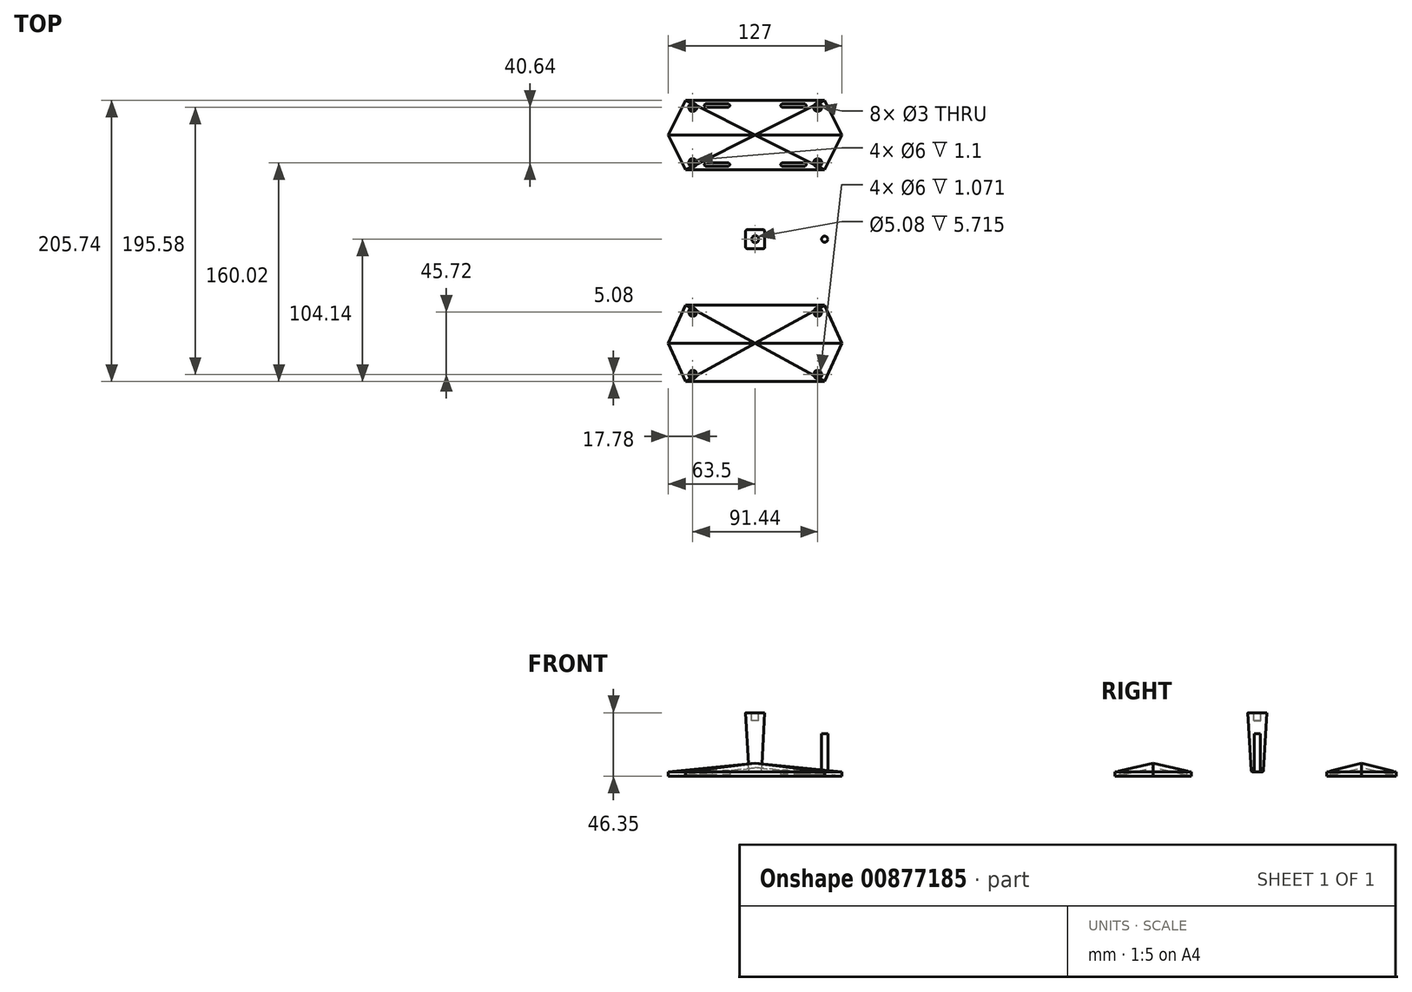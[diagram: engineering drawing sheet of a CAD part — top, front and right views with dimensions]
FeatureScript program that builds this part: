
annotation { "Feature Type Name" : "Feature", "Feature Type Description" : "" }
export const myFeature = defineFeature(function(context is Context, id is Id, definition is map)
    precondition{}
    {
        {
            var Q0;
            Q0=qCreatedBy(makeId("Top.planeOp"),FACE);
            var sketch = newSketch(context, id + "F0", { "sketchPlane" : qUnion([Q0])});
            skLineSegment(sketch, "E0", {"start": v(0, 0) * mm, "end": v(0, -76.2) * mm, "construction": true});
            skLineSegment(sketch, "E1.bottom", {"start": v(50.8, -48.26) * mm, "end": v(-50.8, -48.26) * mm});
            skLineSegment(sketch, "E1.top", {"start": v(50.8, -104.14) * mm, "end": v(-50.8, -104.14) * mm});
            skLineSegment(sketch, "E1.left", {"start": v(50.8, -48.26) * mm, "end": v(50.8, -104.14) * mm, "construction": true});
            skLineSegment(sketch, "E1.right", {"start": v(-50.8, -48.26) * mm, "end": v(-50.8, -104.14) * mm, "construction": true});
            skPoint(sketch, "E1.middle", {"position": v(0, -76.2) * mm});
            skLineSegment(sketch, "E2", {"start": v(50.8, -76.2) * mm, "end": v(63.5, -76.2) * mm, "construction": true});
            skLineSegment(sketch, "E3", {"start": v(63.5, -76.2) * mm, "end": v(50.8, -48.26) * mm});
            skLineSegment(sketch, "E4", {"start": v(50.8, -104.14) * mm, "end": v(63.5, -76.2) * mm});
            skLineSegment(sketch, "E5.MirrorCS", {"start": v(-63.5, -76.2) * mm, "end": v(-50.8, -48.26) * mm});
            skLineSegment(sketch, "E6.MirrorCS", {"start": v(-50.8, -104.14) * mm, "end": v(-63.5, -76.2) * mm});
            skSolve(sketch);
        }
        {
            var Q0;
            Q0=qCreatedBy(makeId("Right.planeOp"),FACE);
            var sketch = newSketch(context, id + "F1", { "sketchPlane" : qUnion([Q0])});
            skLineSegment(sketch, "E7", {"start": v(0, 0) * mm, "end": v(-76.2, 0) * mm, "construction": true});
            skLineSegment(sketch, "E8", {"start": v(-76.2, 0) * mm, "end": v(-76.2, 6.35) * mm, "construction": true});
            skLineSegment(sketch, "E9", {"start": v(-76.2, 0) * mm, "end": v(-76.2, 3.17) * mm, "construction": true});
            skLineSegment(sketch, "E10", {"start": v(0, 0) * mm, "end": v(76.2, 0) * mm, "construction": true});
            skLineSegment(sketch, "E11", {"start": v(76.2, 0) * mm, "end": v(76.2, 6.35) * mm, "construction": true});
            skSolve(sketch);
        }
        {
            var Q0;
            Q0=makeQuery(id+"F0.imprint","IMPRINT",FACE,{"disambiguationData":[TD([[makeQuery(id+"F0.imprint","IMPRINT",EDGE,{"derivedFrom":sQuery(id+"F0.wireOp",EDGE,"E1.bottom")}),1.0]])]});
            var Q1;
            Q1=sQuery(id+"F1.wireOp",VERTEX,"E8.end");
            loft(context, id + "F2", {"sheetProfilesArray" : [{ "sheetProfileEntities" : qUnion([Q0]) }, { "sheetProfileEntities" : qUnion([Q1]) }]});
        }
        {
            var Q0;
            Q0=qCreatedBy(makeId("Right.planeOp"),FACE);
            var sketch = newSketch(context, id + "F3", { "sketchPlane" : qUnion([Q0])});
            skLineSegment(sketch, "E12", {"start": v(0, 0) * mm, "end": v(-76.2, 0) * mm, "construction": true});
            skLineSegment(sketch, "E13", {"start": v(-76.2, 0) * mm, "end": v(-76.2, 3.17) * mm, "construction": true});
            skLineSegment(sketch, "E14", {"start": v(0, 0) * mm, "end": v(76.2, 0) * mm, "construction": true});
            skLineSegment(sketch, "E15", {"start": v(76.2, 0) * mm, "end": v(76.2, 3.18) * mm, "construction": true});
            skSolve(sketch);
        }
        {
            var Q0;
            Q0=qSketchRegion(id+"F0",true);
            extrude(context, id + "F4", {"entities" : qUnion([Q0]), "operationType" : NewBodyOperationType.ADD, "oppositeDirection" : true, "depth" : 3 * mm, "offsetDistance" : 25.4 * mm});
        }
        {
            var Q1;
            Q1=makeQuery(id+"F4.opExtrude","CAP_FACE",FACE,{"disambiguationData":[OSD([sQuery(id+"F0.wireOp",EDGE,"E1.bottom"),sQuery(id+"F0.wireOp",EDGE,"E1.top"),sQuery(id+"F0.wireOp",EDGE,"E3"),sQuery(id+"F0.wireOp",EDGE,"E4"),sQuery(id+"F0.wireOp",EDGE,"E5.MirrorCS"),sQuery(id+"F0.wireOp",EDGE,"E6.MirrorCS")])],"isStart":false});
            var Q2;
            Q2=sQuery(id+"F1.wireOp",VERTEX,"E9.end");
            loft(context, id + "F5", {"operationType" : NewBodyOperationType.REMOVE, "sheetProfilesArray" : [{ "sheetProfileEntities" : qUnion([Q1]) }, { "sheetProfileEntities" : qUnion([Q2]) }]});
        }
        {
            var Q0;
            Q0=qCreatedBy(makeId("Top.planeOp"),FACE);
            var sketch = newSketch(context, id + "F6", { "sketchPlane" : qUnion([Q0])});
            skLineSegment(sketch, "E16", {"start": v(0, 0) * mm, "end": v(0, -76.2) * mm, "construction": true});
            skLineSegment(sketch, "E17", {"start": v(0, -76.2) * mm, "end": v(50.8, -76.2) * mm, "construction": true});
            skLineSegment(sketch, "E18", {"start": v(50.8, -76.2) * mm, "end": v(50.8, -48.26) * mm, "construction": true});
            skLineSegment(sketch, "E19.bottom", {"start": v(50.8, -48.26) * mm, "end": v(45.72, -48.26) * mm, "construction": true});
            skLineSegment(sketch, "E19.top", {"start": v(50.8, -53.34) * mm, "end": v(45.72, -53.34) * mm, "construction": true});
            skLineSegment(sketch, "E19.left", {"start": v(50.8, -48.26) * mm, "end": v(50.8, -53.34) * mm, "construction": true});
            skLineSegment(sketch, "E19.right", {"start": v(45.72, -48.26) * mm, "end": v(45.72, -53.34) * mm, "construction": true});
            skCircle(sketch, "E20", {"center": v(45.72, -53.34) * mm, "radius": 1.5 * mm});
            skCircle(sketch, "E21.MirrorC", {"center": v(-45.72, -53.34) * mm, "radius": 1.5 * mm});
            skCircle(sketch, "E22.MirrorC", {"center": v(45.72, -99.06) * mm, "radius": 1.5 * mm});
            skCircle(sketch, "E23.MirrorC", {"center": v(-45.72, -99.06) * mm, "radius": 1.5 * mm});
            skSolve(sketch);
        }
        {
            var Q0;
            Q0=makeQuery(id+"F6.imprint","IMPRINT",FACE,{"disambiguationData":[TD([[makeQuery(id+"F6.imprint","IMPRINT",EDGE,{"derivedFrom":sQuery(id+"F6.wireOp",EDGE,"E20")}),1.0]])]});
            var Q1;
            Q1=makeQuery(id+"F6.imprint","IMPRINT",FACE,{"disambiguationData":[TD([[makeQuery(id+"F6.imprint","IMPRINT",EDGE,{"derivedFrom":sQuery(id+"F6.wireOp",EDGE,"E21.MirrorC")}),-1.0]])]});
            var Q2;
            Q2=makeQuery(id+"F6.imprint","IMPRINT",FACE,{"disambiguationData":[TD([[makeQuery(id+"F6.imprint","IMPRINT",EDGE,{"derivedFrom":sQuery(id+"F6.wireOp",EDGE,"E22.MirrorC")}),-1.0]])]});
            var Q3;
            Q3=makeQuery(id+"F6.imprint","IMPRINT",FACE,{"disambiguationData":[TD([[makeQuery(id+"F6.imprint","IMPRINT",EDGE,{"derivedFrom":sQuery(id+"F6.wireOp",EDGE,"E23.MirrorC")}),1.0]])]});
            var Q4;
            Q4=makeQuery(id+"F6.imprint","IMPRINT",FACE,{"disambiguationData":[TD([[makeQuery(id+"F6.imprint","IMPRINT",EDGE,{"derivedFrom":sQuery(id+"F6.wireOp",EDGE,"608550e4-dcd5-4afd-8712-c4d8ff7671cc0.MirrorC")}),-1.0]])]});
            var Q5;
            Q5=makeQuery(id+"F6.imprint","IMPRINT",FACE,{"disambiguationData":[TD([[makeQuery(id+"F6.imprint","IMPRINT",EDGE,{"derivedFrom":sQuery(id+"F6.wireOp",EDGE,"e33e717c-8c95-4304-aaaf-b1c399a1f4810.MirrorC")}),-1.0]])]});
            var Q6;
            Q6=makeQuery(id+"F6.imprint","IMPRINT",FACE,{"disambiguationData":[TD([[makeQuery(id+"F6.imprint","IMPRINT",EDGE,{"derivedFrom":sQuery(id+"F6.wireOp",EDGE,"5184385d-e241-4d37-b116-434bd50265c70.MirrorC")}),1.0]])]});
            var Q7;
            Q7=makeQuery(id+"F6.imprint","IMPRINT",FACE,{"disambiguationData":[TD([[makeQuery(id+"F6.imprint","IMPRINT",EDGE,{"derivedFrom":sQuery(id+"F6.wireOp",EDGE,"1d585823-e6b4-4162-827a-ad62070646b00.MirrorC")}),1.0]])]});
            extrude(context, id + "F7", {"entities" : qUnion([Q0, Q1, Q2, Q3, Q4, Q5, Q6, Q7]), "operationType" : NewBodyOperationType.REMOVE, "depth" : 25.4 * mm, "offsetDistance" : 25.4 * mm});
        }
        {
            var Q0;
            Q0=qSketchRegion(id+"F6",true);
            extrude(context, id + "F8", {"entities" : qUnion([Q0]), "operationType" : NewBodyOperationType.REMOVE, "oppositeDirection" : true, "depth" : 25.4 * mm, "offsetDistance" : 25.4 * mm});
        }
        {
            var Q0;
            Q0=qCreatedBy(makeId("Top.planeOp"),FACE);
            var sketch = newSketch(context, id + "F9", { "sketchPlane" : qUnion([Q0])});
            skLineSegment(sketch, "E24", {"start": v(0, 0) * mm, "end": v(0, -76.2) * mm, "construction": true});
            skLineSegment(sketch, "E25", {"start": v(0, -76.2) * mm, "end": v(50.8, -76.2) * mm, "construction": true});
            skLineSegment(sketch, "E26", {"start": v(50.8, -76.2) * mm, "end": v(50.8, -48.26) * mm, "construction": true});
            skLineSegment(sketch, "E27.bottom", {"start": v(50.8, -48.26) * mm, "end": v(45.72, -48.26) * mm, "construction": true});
            skLineSegment(sketch, "E27.top", {"start": v(50.8, -53.34) * mm, "end": v(45.72, -53.34) * mm, "construction": true});
            skLineSegment(sketch, "E27.left", {"start": v(50.8, -48.26) * mm, "end": v(50.8, -53.34) * mm, "construction": true});
            skLineSegment(sketch, "E27.right", {"start": v(45.72, -48.26) * mm, "end": v(45.72, -53.34) * mm, "construction": true});
            skCircle(sketch, "E28", {"center": v(45.72, -53.34) * mm, "radius": 3 * mm});
            skCircle(sketch, "E29", {"center": v(45.72, -53.34) * mm, "radius": 1.5 * mm});
            skCircle(sketch, "E30.MirrorC", {"center": v(45.72, -99.06) * mm, "radius": 1.5 * mm});
            skCircle(sketch, "E31.MirrorC", {"center": v(45.72, -99.06) * mm, "radius": 3 * mm});
            skCircle(sketch, "E32.MirrorC", {"center": v(-45.72, -53.34) * mm, "radius": 3 * mm});
            skCircle(sketch, "E33.MirrorC", {"center": v(-45.72, -53.34) * mm, "radius": 1.5 * mm});
            skCircle(sketch, "E34.MirrorC", {"center": v(-45.72, -99.06) * mm, "radius": 1.5 * mm});
            skCircle(sketch, "E35.MirrorC", {"center": v(-45.72, -99.06) * mm, "radius": 3 * mm});
            skSolve(sketch);
        }
        {
            var Q0;
            Q0=qSketchRegion(id+"F9",true);
            extrude(context, id + "F10", {"entities" : qUnion([Q0]), "operationType" : NewBodyOperationType.ADD, "oppositeDirection" : true, "depth" : 3 * mm, "offsetDistance" : 25.4 * mm});
        }
        {
            var Q0;
            Q0=qCreatedBy(makeId("Top.planeOp"),FACE);
            var sketch = newSketch(context, id + "F11", { "sketchPlane" : qUnion([Q0])});
            skLineSegment(sketch, "E36.bottom", {"start": v(4.45, 4.45) * mm, "end": v(-4.44, 4.45) * mm});
            skLineSegment(sketch, "E36.top", {"start": v(4.44, -4.45) * mm, "end": v(-4.45, -4.45) * mm});
            skLineSegment(sketch, "E36.left", {"start": v(4.45, 4.45) * mm, "end": v(4.45, -4.45) * mm});
            skLineSegment(sketch, "E36.right", {"start": v(-4.45, 4.45) * mm, "end": v(-4.45, -4.45) * mm});
            skPoint(sketch, "E36.middle", {"position": v(0, 0) * mm});
            skSolve(sketch);
        }
        {
            var Q0;
            Q0=qCreatedBy(makeId("Top.planeOp"),FACE);
            cPlane(context, id + "F12", {"entities" : qUnion([Q0]), "cplaneType" : CPlaneType.OFFSET, "offset" : 28 * mm + 6.35 * mm + 3 * mm + 6 * mm, "width" : 152.4 * mm, "height" : 152.4 * mm});
        }
        {
            var Q0;
            Q0=qCreatedBy(id+"F12.planeOp",FACE);
            var sketch = newSketch(context, id + "F13", { "sketchPlane" : qUnion([Q0])});
            skLineSegment(sketch, "E37.bottom", {"start": v(6.99, 6.99) * mm, "end": v(-6.99, 6.99) * mm});
            skLineSegment(sketch, "E37.top", {"start": v(6.99, -6.99) * mm, "end": v(-6.99, -6.99) * mm});
            skLineSegment(sketch, "E37.left", {"start": v(6.99, 6.99) * mm, "end": v(6.99, -6.99) * mm});
            skLineSegment(sketch, "E37.right", {"start": v(-6.99, 6.99) * mm, "end": v(-6.99, -6.99) * mm});
            skPoint(sketch, "E37.middle", {"position": v(0, 0) * mm});
            skSolve(sketch);
        }
        {
            var Q0;
            Q0=makeQuery(id+"F11.imprint","IMPRINT",FACE,{"disambiguationData":[TD([[makeQuery(id+"F11.imprint","IMPRINT",EDGE,{"derivedFrom":sQuery(id+"F11.wireOp",EDGE,"E36.bottom")}),1.0]])]});
            var Q1;
            Q1=makeQuery(id+"F13.imprint","IMPRINT",FACE,{"disambiguationData":[TD([[makeQuery(id+"F13.imprint","IMPRINT",EDGE,{"derivedFrom":sQuery(id+"F13.wireOp",EDGE,"E37.bottom")}),1.0]])]});
            loft(context, id + "F14", {"sheetProfilesArray" : [{ "sheetProfileEntities" : qUnion([Q0]) }, { "sheetProfileEntities" : qUnion([Q1]) }]});
        }
        {
            var Q0;
            Q0=makeQuery(id+"F14.opLoft","MID_CAP_EDGE",EDGE,{"disambiguationData":[OSD([sQuery(id+"F11.wireOp",EDGE,"E36.top"),sQuery(id+"F11.wireOp",EDGE,"E36.left"),sQuery(id+"F11.wireOp",EDGE,"E36.right")])],"capPos":0.0});
            var Q1;
            Q1=makeQuery(id+"F14.opLoft","MID_CAP_EDGE",EDGE,{"disambiguationData":[OSD([sQuery(id+"F11.wireOp",EDGE,"E36.bottom"),sQuery(id+"F11.wireOp",EDGE,"E36.left"),sQuery(id+"F11.wireOp",EDGE,"E36.right")])],"capPos":0.0});
            var Q2;
            Q2=makeQuery(id+"F14.opLoft","MID_CAP_EDGE",EDGE,{"disambiguationData":[OSD([sQuery(id+"F11.wireOp",EDGE,"E36.bottom"),sQuery(id+"F11.wireOp",EDGE,"E36.top"),sQuery(id+"F11.wireOp",EDGE,"E36.left")])],"capPos":0.0});
            var Q3;
            Q3=makeQuery(id+"F14.opLoft","MID_CAP_EDGE",EDGE,{"disambiguationData":[OSD([sQuery(id+"F11.wireOp",EDGE,"E36.bottom"),sQuery(id+"F11.wireOp",EDGE,"E36.top"),sQuery(id+"F11.wireOp",EDGE,"E36.right")])],"capPos":0.0});
            var Q4;
            Q4=makeQuery(id+"F14.opLoft","SWEPT_EDGE",EDGE,{"disambiguationData":[OSD([sQuery(id+"F11.wireOp",EDGE,"E36.top"),sQuery(id+"F11.wireOp",EDGE,"E36.left"),sQuery(id+"F13.wireOp",EDGE,"E37.top"),sQuery(id+"F13.wireOp",EDGE,"E37.left")])]});
            var Q5;
            Q5=makeQuery(id+"F14.opLoft","SWEPT_EDGE",EDGE,{"disambiguationData":[OSD([sQuery(id+"F11.wireOp",EDGE,"E36.top"),sQuery(id+"F11.wireOp",EDGE,"E36.right"),sQuery(id+"F13.wireOp",EDGE,"E37.top"),sQuery(id+"F13.wireOp",EDGE,"E37.right")])]});
            var Q6;
            Q6=makeQuery(id+"F14.opLoft","SWEPT_EDGE",EDGE,{"disambiguationData":[OSD([sQuery(id+"F11.wireOp",EDGE,"E36.bottom"),sQuery(id+"F11.wireOp",EDGE,"E36.right"),sQuery(id+"F13.wireOp",EDGE,"E37.bottom"),sQuery(id+"F13.wireOp",EDGE,"E37.right")])]});
            var Q7;
            Q7=makeQuery(id+"F14.opLoft","SWEPT_EDGE",EDGE,{"disambiguationData":[OSD([sQuery(id+"F11.wireOp",EDGE,"E36.bottom"),sQuery(id+"F11.wireOp",EDGE,"E36.left"),sQuery(id+"F13.wireOp",EDGE,"E37.bottom"),sQuery(id+"F13.wireOp",EDGE,"E37.left")])]});
            fillet(context, id + "F15", {"entities" : qUnion([Q0, Q1, Q2, Q3, Q4, Q5, Q6, Q7]), "radius" : 1.27 * mm, "tangentPropagation" : true, "allowEdgeOverflow" : false});
        }
        {
            var Q0;
            Q0=qCreatedBy(makeId("Top.planeOp"),FACE);
            var sketch = newSketch(context, id + "F16", { "sketchPlane" : qUnion([Q0])});
            skLineSegment(sketch, "E38", {"start": v(0, 0) * mm, "end": v(50.8, 0) * mm, "construction": true});
            skCircle(sketch, "E39", {"center": v(50.8, 0) * mm, "radius": 2.25 * mm});
            skSolve(sketch);
        }
        {
            var Q0;
            Q0=qSketchRegion(id+"F16",true);
            extrude(context, id + "F17", {"entities" : qUnion([Q0]), "depth" : 28 * mm, "offsetDistance" : 25.4 * mm});
        }
        {
            var Q0;
            Q0=qCreatedBy(makeId("Top.planeOp"),FACE);
            var sketch = newSketch(context, id + "F18", { "sketchPlane" : qUnion([Q0])});
            skLineSegment(sketch, "E40", {"start": v(0, 0) * mm, "end": v(0, 76.2) * mm, "construction": true});
            skLineSegment(sketch, "E41.bottom", {"start": v(50.8, 50.8) * mm, "end": v(-50.8, 50.8) * mm});
            skLineSegment(sketch, "E41.top", {"start": v(50.8, 101.6) * mm, "end": v(-50.8, 101.6) * mm});
            skLineSegment(sketch, "E41.left", {"start": v(50.8, 50.8) * mm, "end": v(50.8, 101.6) * mm, "construction": true});
            skLineSegment(sketch, "E41.right", {"start": v(-50.8, 50.8) * mm, "end": v(-50.8, 101.6) * mm, "construction": true});
            skPoint(sketch, "E41.middle", {"position": v(0, 76.2) * mm});
            skLineSegment(sketch, "E42", {"start": v(50.8, 76.2) * mm, "end": v(63.5, 76.2) * mm, "construction": true});
            skLineSegment(sketch, "E43", {"start": v(63.5, 76.2) * mm, "end": v(50.8, 101.6) * mm});
            skLineSegment(sketch, "E44", {"start": v(50.8, 50.8) * mm, "end": v(63.5, 76.2) * mm});
            skLineSegment(sketch, "E45.MirrorCS", {"start": v(-50.8, 50.8) * mm, "end": v(-63.5, 76.2) * mm});
            skLineSegment(sketch, "E46.MirrorCS", {"start": v(-63.5, 76.2) * mm, "end": v(-50.8, 101.6) * mm});
            skSolve(sketch);
        }
        {
            var Q0;
            Q0=makeQuery(id+"F18.imprint","IMPRINT",FACE,{"disambiguationData":[TD([[makeQuery(id+"F18.imprint","IMPRINT",EDGE,{"derivedFrom":sQuery(id+"F18.wireOp",EDGE,"E41.bottom")}),-1.0]])]});
            var Q1;
            Q1=sQuery(id+"F1.wireOp",VERTEX,"E11.end");
            loft(context, id + "F19", {"sheetProfilesArray" : [{ "sheetProfileEntities" : qUnion([Q0]) }, { "sheetProfileEntities" : qUnion([Q1]) }]});
        }
        {
            var Q0;
            Q0=qSketchRegion(id+"F18",true);
            extrude(context, id + "F20", {"entities" : qUnion([Q0]), "operationType" : NewBodyOperationType.ADD, "oppositeDirection" : true, "depth" : 3 * mm, "offsetDistance" : 25.4 * mm});
        }
        {
            var Q1;
            Q1=makeQuery(id+"F20.opExtrude","CAP_FACE",FACE,{"disambiguationData":[OSD([sQuery(id+"F18.wireOp",EDGE,"E41.bottom"),sQuery(id+"F18.wireOp",EDGE,"E41.top"),sQuery(id+"F18.wireOp",EDGE,"E43"),sQuery(id+"F18.wireOp",EDGE,"E44"),sQuery(id+"F18.wireOp",EDGE,"E45.MirrorCS"),sQuery(id+"F18.wireOp",EDGE,"E46.MirrorCS")])],"isStart":false});
            var Q2;
            Q2=sQuery(id+"F3.wireOp",VERTEX,"E15.end");
            loft(context, id + "F21", {"operationType" : NewBodyOperationType.REMOVE, "sheetProfilesArray" : [{ "sheetProfileEntities" : qUnion([Q1]) }, { "sheetProfileEntities" : qUnion([Q2]) }]});
        }
        {
            var Q0;
            Q0=qCreatedBy(makeId("Top.planeOp"),FACE);
            var sketch = newSketch(context, id + "F22", { "sketchPlane" : qUnion([Q0])});
            skLineSegment(sketch, "E47", {"start": v(0, 0) * mm, "end": v(0, 76.2) * mm, "construction": true});
            skLineSegment(sketch, "E48", {"start": v(0, 76.2) * mm, "end": v(-50.8, 76.2) * mm, "construction": true});
            skLineSegment(sketch, "E49", {"start": v(-50.8, 76.2) * mm, "end": v(-50.8, 50.8) * mm, "construction": true});
            skLineSegment(sketch, "E50.bottom", {"start": v(-50.8, 50.8) * mm, "end": v(-45.72, 50.8) * mm, "construction": true});
            skLineSegment(sketch, "E50.top", {"start": v(-50.8, 55.88) * mm, "end": v(-45.72, 55.88) * mm, "construction": true});
            skLineSegment(sketch, "E50.left", {"start": v(-50.8, 50.8) * mm, "end": v(-50.8, 55.88) * mm, "construction": true});
            skLineSegment(sketch, "E50.right", {"start": v(-45.72, 50.8) * mm, "end": v(-45.72, 55.88) * mm, "construction": true});
            skCircle(sketch, "E51", {"center": v(-45.72, 55.88) * mm, "radius": 1.5 * mm});
            skCircle(sketch, "E52.MirrorC", {"center": v(45.72, 55.88) * mm, "radius": 1.5 * mm});
            skCircle(sketch, "E53.MirrorC", {"center": v(-45.72, 96.52) * mm, "radius": 1.5 * mm});
            skCircle(sketch, "E54.MirrorC", {"center": v(45.72, 96.52) * mm, "radius": 1.5 * mm});
            skSolve(sketch);
        }
        {
            var Q0;
            Q0=qSketchRegion(id+"F22",true);
            extrude(context, id + "F23", {"entities" : qUnion([Q0]), "operationType" : NewBodyOperationType.REMOVE, "oppositeDirection" : true, "depth" : 25.4 * mm, "offsetDistance" : 25.4 * mm, "symmetric" : true});
        }
        {
            var Q0;
            Q0=qCreatedBy(makeId("Top.planeOp"),FACE);
            var sketch = newSketch(context, id + "F24", { "sketchPlane" : qUnion([Q0])});
            skLineSegment(sketch, "E55", {"start": v(0, 0) * mm, "end": v(0, 76.2) * mm, "construction": true});
            skLineSegment(sketch, "E56", {"start": v(0, 76.2) * mm, "end": v(50.8, 76.2) * mm, "construction": true});
            skLineSegment(sketch, "E57", {"start": v(50.8, 76.2) * mm, "end": v(50.8, 50.8) * mm, "construction": true});
            skLineSegment(sketch, "E58.bottom", {"start": v(50.8, 50.8) * mm, "end": v(45.72, 50.8) * mm, "construction": true});
            skLineSegment(sketch, "E58.top", {"start": v(50.8, 55.88) * mm, "end": v(45.72, 55.88) * mm, "construction": true});
            skLineSegment(sketch, "E58.left", {"start": v(50.8, 50.8) * mm, "end": v(50.8, 55.88) * mm, "construction": true});
            skLineSegment(sketch, "E58.right", {"start": v(45.72, 50.8) * mm, "end": v(45.72, 55.88) * mm, "construction": true});
            skCircle(sketch, "E59", {"center": v(45.72, 55.88) * mm, "radius": 1.5 * mm});
            skCircle(sketch, "E60", {"center": v(45.72, 55.88) * mm, "radius": 3 * mm});
            skCircle(sketch, "E61.MirrorC", {"center": v(45.72, 96.52) * mm, "radius": 1.5 * mm});
            skCircle(sketch, "E62.MirrorC", {"center": v(45.72, 96.52) * mm, "radius": 3 * mm});
            skCircle(sketch, "E63.MirrorC", {"center": v(-45.72, 55.88) * mm, "radius": 3 * mm});
            skCircle(sketch, "E64.MirrorC", {"center": v(-45.72, 55.88) * mm, "radius": 1.5 * mm});
            skCircle(sketch, "E65.MirrorC", {"center": v(-45.72, 96.52) * mm, "radius": 1.5 * mm});
            skCircle(sketch, "E66.MirrorC", {"center": v(-45.72, 96.52) * mm, "radius": 3 * mm});
            skSolve(sketch);
        }
        {
            var Q0;
            Q0=qSketchRegion(id+"F24",true);
            extrude(context, id + "F25", {"entities" : qUnion([Q0]), "operationType" : NewBodyOperationType.ADD, "oppositeDirection" : true, "depth" : 3 * mm, "offsetDistance" : 25.4 * mm});
        }
        {
            var Q0;
            Q0=qCreatedBy(makeId("Top.planeOp"),FACE);
            var sketch = newSketch(context, id + "F26", { "sketchPlane" : qUnion([Q0])});
            skLineSegment(sketch, "E67", {"start": v(0, 0) * mm, "end": v(0, 76.2) * mm, "construction": true});
            skLineSegment(sketch, "E68", {"start": v(0, 76.2) * mm, "end": v(27.94, 76.2) * mm, "construction": true});
            skLineSegment(sketch, "E69", {"start": v(27.94, 76.2) * mm, "end": v(27.94, 54.61) * mm});
            skLineSegment(sketch, "E70.bottom", {"start": v(37.47, 53.34) * mm, "end": v(18.42, 53.34) * mm});
            skLineSegment(sketch, "E70.top", {"start": v(37.47, 55.88) * mm, "end": v(18.42, 55.88) * mm});
            skLineSegment(sketch, "E70.left", {"start": v(37.47, 53.34) * mm, "end": v(37.47, 55.88) * mm});
            skLineSegment(sketch, "E70.right", {"start": v(18.42, 53.34) * mm, "end": v(18.42, 55.88) * mm});
            skPoint(sketch, "E70.middle", {"position": v(27.94, 54.61) * mm});
            skLineSegment(sketch, "E71.MirrorCS", {"start": v(37.47, 96.52) * mm, "end": v(18.42, 96.52) * mm});
            skLineSegment(sketch, "E72.MirrorCS", {"start": v(18.42, 99.06) * mm, "end": v(18.42, 96.52) * mm});
            skLineSegment(sketch, "E73.MirrorCS", {"start": v(37.47, 99.06) * mm, "end": v(18.42, 99.06) * mm});
            skLineSegment(sketch, "E74.MirrorCS", {"start": v(37.47, 99.06) * mm, "end": v(37.47, 96.52) * mm});
            skLineSegment(sketch, "E75.MirrorCS", {"start": v(-37.47, 96.52) * mm, "end": v(-18.42, 96.52) * mm});
            skLineSegment(sketch, "E76.MirrorCS", {"start": v(-18.42, 99.06) * mm, "end": v(-18.42, 96.52) * mm});
            skLineSegment(sketch, "E77.MirrorCS", {"start": v(-37.47, 99.06) * mm, "end": v(-18.42, 99.06) * mm});
            skLineSegment(sketch, "E78.MirrorCS", {"start": v(-37.47, 99.06) * mm, "end": v(-37.47, 96.52) * mm});
            skLineSegment(sketch, "E79.MirrorCS", {"start": v(-37.47, 53.34) * mm, "end": v(-37.47, 55.88) * mm});
            skLineSegment(sketch, "E80.MirrorCS", {"start": v(-37.47, 55.88) * mm, "end": v(-18.41, 55.88) * mm});
            skLineSegment(sketch, "E81.MirrorCS", {"start": v(-18.42, 53.34) * mm, "end": v(-18.42, 55.88) * mm});
            skLineSegment(sketch, "E82.MirrorCS", {"start": v(-37.47, 53.34) * mm, "end": v(-18.41, 53.34) * mm});
            skSolve(sketch);
        }
        {
            var Q0;
            Q0=qSketchRegion(id+"F26",true);
            extrude(context, id + "F27", {"entities" : qUnion([Q0]), "operationType" : NewBodyOperationType.REMOVE, "oppositeDirection" : true, "depth" : 25.4 * mm, "offsetDistance" : 25.4 * mm, "symmetric" : true});
        }
        {
            var Q0;
            Q0=makeQuery(id+"F27.boolean.opBoolean","COPY",EDGE,{"derivedFrom":makeQuery(id+"F27.opExtrude","SWEPT_EDGE",EDGE,{"disambiguationData":[OSD([sQuery(id+"F26.wireOp",EDGE,"E75.MirrorCS"),sQuery(id+"F26.wireOp",EDGE,"E76.MirrorCS")])]})});
            var Q1;
            Q1=makeQuery(id+"F27.boolean.opBoolean","COPY",EDGE,{"derivedFrom":makeQuery(id+"F27.opExtrude","SWEPT_EDGE",EDGE,{"disambiguationData":[OSD([sQuery(id+"F26.wireOp",EDGE,"E71.MirrorCS"),sQuery(id+"F26.wireOp",EDGE,"E74.MirrorCS")])]})});
            var Q2;
            Q2=makeQuery(id+"F27.boolean.opBoolean","COPY",EDGE,{"derivedFrom":makeQuery(id+"F27.opExtrude","SWEPT_EDGE",EDGE,{"disambiguationData":[OSD([sQuery(id+"F26.wireOp",EDGE,"E81.MirrorCS"),sQuery(id+"F26.wireOp",EDGE,"E82.MirrorCS")])]})});
            var Q3;
            Q3=makeQuery(id+"F27.boolean.opBoolean","COPY",EDGE,{"derivedFrom":makeQuery(id+"F27.opExtrude","SWEPT_EDGE",EDGE,{"disambiguationData":[OSD([sQuery(id+"F26.wireOp",EDGE,"E70.bottom"),sQuery(id+"F26.wireOp",EDGE,"E70.left")])]})});
            var Q4;
            Q4=makeQuery(id+"F27.boolean.opBoolean","COPY",EDGE,{"derivedFrom":makeQuery(id+"F27.opExtrude","SWEPT_EDGE",EDGE,{"disambiguationData":[OSD([sQuery(id+"F26.wireOp",EDGE,"E77.MirrorCS"),sQuery(id+"F26.wireOp",EDGE,"E78.MirrorCS")])]})});
            var Q5;
            Q5=makeQuery(id+"F27.boolean.opBoolean","COPY",EDGE,{"derivedFrom":makeQuery(id+"F27.opExtrude","SWEPT_EDGE",EDGE,{"disambiguationData":[OSD([sQuery(id+"F26.wireOp",EDGE,"E72.MirrorCS"),sQuery(id+"F26.wireOp",EDGE,"E73.MirrorCS")])]})});
            var Q6;
            Q6=makeQuery(id+"F27.boolean.opBoolean","COPY",EDGE,{"derivedFrom":makeQuery(id+"F27.opExtrude","SWEPT_EDGE",EDGE,{"disambiguationData":[OSD([sQuery(id+"F26.wireOp",EDGE,"E70.top"),sQuery(id+"F26.wireOp",EDGE,"E70.right")])]})});
            var Q7;
            Q7=makeQuery(id+"F27.boolean.opBoolean","COPY",EDGE,{"derivedFrom":makeQuery(id+"F27.opExtrude","SWEPT_EDGE",EDGE,{"disambiguationData":[OSD([sQuery(id+"F26.wireOp",EDGE,"E79.MirrorCS"),sQuery(id+"F26.wireOp",EDGE,"E80.MirrorCS")])]})});
            var Q8;
            Q8=makeQuery(id+"F27.boolean.opBoolean","COPY",EDGE,{"derivedFrom":makeQuery(id+"F27.opExtrude","SWEPT_EDGE",EDGE,{"disambiguationData":[OSD([sQuery(id+"F26.wireOp",EDGE,"E76.MirrorCS"),sQuery(id+"F26.wireOp",EDGE,"E77.MirrorCS")])]})});
            var Q9;
            Q9=makeQuery(id+"F27.boolean.opBoolean","COPY",EDGE,{"derivedFrom":makeQuery(id+"F27.opExtrude","SWEPT_EDGE",EDGE,{"disambiguationData":[OSD([sQuery(id+"F26.wireOp",EDGE,"E73.MirrorCS"),sQuery(id+"F26.wireOp",EDGE,"E74.MirrorCS")])]})});
            var Q10;
            Q10=makeQuery(id+"F27.boolean.opBoolean","COPY",EDGE,{"derivedFrom":makeQuery(id+"F27.opExtrude","SWEPT_EDGE",EDGE,{"disambiguationData":[OSD([sQuery(id+"F26.wireOp",EDGE,"E80.MirrorCS"),sQuery(id+"F26.wireOp",EDGE,"E81.MirrorCS")])]})});
            var Q11;
            Q11=makeQuery(id+"F27.boolean.opBoolean","COPY",EDGE,{"derivedFrom":makeQuery(id+"F27.opExtrude","SWEPT_EDGE",EDGE,{"disambiguationData":[OSD([sQuery(id+"F26.wireOp",EDGE,"E70.top"),sQuery(id+"F26.wireOp",EDGE,"E70.left")])]})});
            var Q12;
            Q12=makeQuery(id+"F27.boolean.opBoolean","COPY",EDGE,{"derivedFrom":makeQuery(id+"F27.opExtrude","SWEPT_EDGE",EDGE,{"disambiguationData":[OSD([sQuery(id+"F26.wireOp",EDGE,"E70.bottom"),sQuery(id+"F26.wireOp",EDGE,"E70.right")])]})});
            var Q13;
            Q13=makeQuery(id+"F27.boolean.opBoolean","COPY",EDGE,{"derivedFrom":makeQuery(id+"F27.opExtrude","SWEPT_EDGE",EDGE,{"disambiguationData":[OSD([sQuery(id+"F26.wireOp",EDGE,"E79.MirrorCS"),sQuery(id+"F26.wireOp",EDGE,"E82.MirrorCS")])]})});
            var Q14;
            Q14=makeQuery(id+"F27.boolean.opBoolean","COPY",EDGE,{"derivedFrom":makeQuery(id+"F27.opExtrude","SWEPT_EDGE",EDGE,{"disambiguationData":[OSD([sQuery(id+"F26.wireOp",EDGE,"E75.MirrorCS"),sQuery(id+"F26.wireOp",EDGE,"E78.MirrorCS")])]})});
            var Q15;
            Q15=makeQuery(id+"F27.boolean.opBoolean","COPY",EDGE,{"derivedFrom":makeQuery(id+"F27.opExtrude","SWEPT_EDGE",EDGE,{"disambiguationData":[OSD([sQuery(id+"F26.wireOp",EDGE,"E71.MirrorCS"),sQuery(id+"F26.wireOp",EDGE,"E72.MirrorCS")])]})});
            fillet(context, id + "F28", {"entities" : qUnion([Q0, Q1, Q2, Q3, Q4, Q5, Q6, Q7, Q8, Q9, Q10, Q11, Q12, Q13, Q14, Q15]), "radius" : 1.9 * mm, "tangentPropagation" : true, "allowEdgeOverflow" : false});
        }
        {
            var Q0;
            Q0=makeQuery(id+"F14.opLoft","CAP_FACE",FACE,{"disambiguationData":[OSD([makeQuery(id+"F13.imprint","IMPRINT",FACE,{"disambiguationData":[TD([[makeQuery(id+"F13.imprint","IMPRINT",EDGE,{"derivedFrom":sQuery(id+"F13.wireOp",EDGE,"E37.bottom")}),1.0]])]})])],"isStart":true});
            var sketch = newSketch(context, id + "F29", { "sketchPlane" : qUnion([Q0])});
            skCircle(sketch, "E83", {"center": v(0, 0) * mm, "radius": 2.54 * mm});
            skSolve(sketch);
        }
        {
            var Q0;
            Q0=qSketchRegion(id+"F29",true);
            extrude(context, id + "F30", {"entities" : qUnion([Q0]), "operationType" : NewBodyOperationType.REMOVE, "oppositeDirection" : true, "depth" : 5.7 * mm, "offsetDistance" : 25.4 * mm});
        }
        {
            var Q0;
            Q0=qSketchRegion(id+"F9",true);
            extrude(context, id + "F31", {"entities" : qUnion([Q0]), "operationType" : NewBodyOperationType.REMOVE, "depth" : 25.4 * mm, "offsetDistance" : 25.4 * mm});
        }
        {
            var Q0;
            Q0=qSketchRegion(id+"F24",true);
            extrude(context, id + "F32", {"entities" : qUnion([Q0]), "operationType" : NewBodyOperationType.REMOVE, "depth" : 25.4 * mm, "offsetDistance" : 25.4 * mm});
        }
    });
